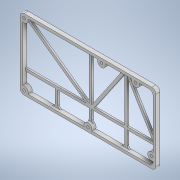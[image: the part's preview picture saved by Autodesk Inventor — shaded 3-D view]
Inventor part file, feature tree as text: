
AUTODESK INVENTOR PART (.ipt)
format: ipt  version: 2021 (Build 250183000, 183)  size: 300,544 bytes
history: native  units: mm
features: sketch x5, extrude x4, fillet x3, hole x1
ambient origin geometry x8: Origin, YZ Plane, XZ Plane, XY Plane, X Axis, Y Axis, Z Axis, Center Point
bodies: Solid1 (feature_tree)
feature tree (13):
  extrude  "Extrusion1"  Depth=52.0mm
  fillet  "Fillet1"  Radius=2.0mm
  extrude  "Extrusion2"  Depth=2.0mm
  hole  "Hole1"  [1 undecoded]
  extrude  "Extrusion3"  Depth=3.0mm
  extrude  "Extrusion4"  Depth=3.0mm
  fillet  "Fillet2"  Radius=50.0mm
  fillet  "Fillet3"  Radius=8.0mm
  sketch  "Sketch1"  dims[d0=100.0mm d1=52.0mm d2=2.0mm]
  sketch  "Sketch2"  dims[d3=2.0mm d4=2.0mm]
  sketch  "Sketch3"  dims[d5=2.0mm d6=3.0mm d7=0.0mm]
  sketch  "Sketch4"  dims[d8=3.0mm d9=3.0mm]
  sketch  "Sketch5"  dims[d10=3.0mm d11=3.0mm d12=50.0mm d13=8.0mm d14=97.0mm d15=3.0mm d16=49.0mm d17=60.0mm d18=49.0mm d19=85.0mm d20=49.0mm d21=6.0mm d22=6.0mm d23=6.0mm d24=6.0mm d25=6.0mm d26=3.0mm d27=0.0mm d28=2.0mm d29=6.0mm d30=4.0mm d31=2.0mm d32=90.0deg d33=4.0mm d34=20.594885mm d35=24.0mm d36=2.0mm d37=2.0mm d38=15.0mm d39=15.0mm d40=2.0mm d41=2.0mm d42=2.0mm d43=2.0mm d44=2.0mm d45=1.2mm d46=0.0mm d47=25.0mm d48=2.0mm d49=1.2mm d50=0.0mm d51=2.0mm d52=2.0mm]
note: 1 required parameter value undecoded (feature->parameter linkage not recoverable at this tier; creation-order binding heuristic only, values carry confidence <= 0.55)
